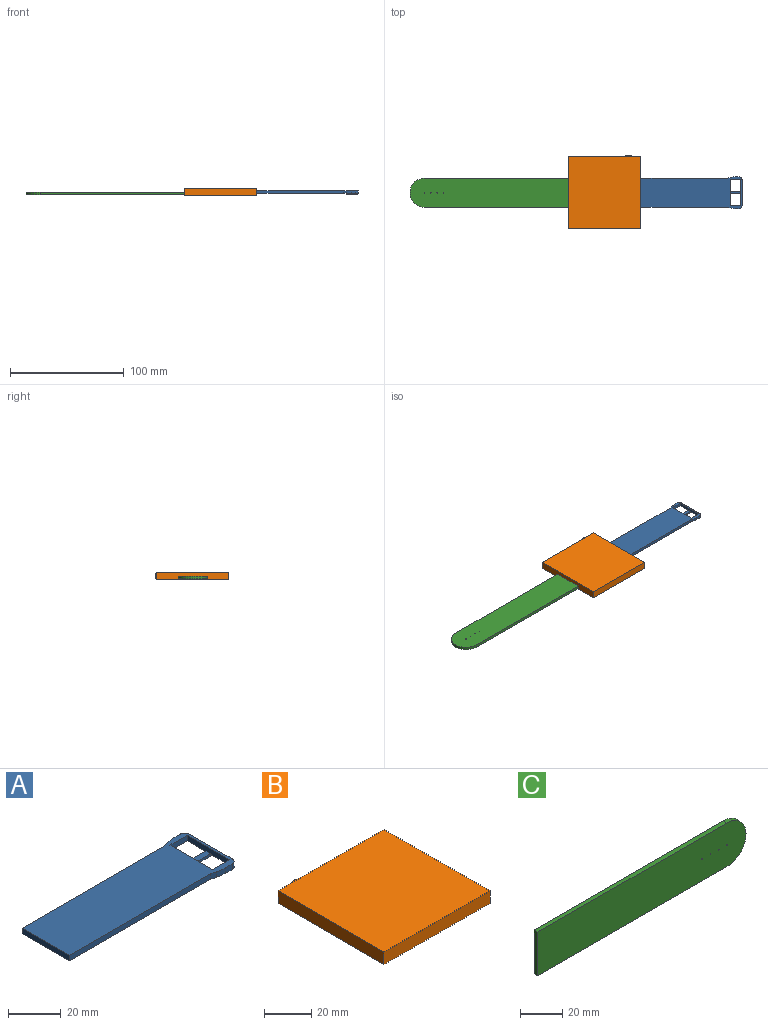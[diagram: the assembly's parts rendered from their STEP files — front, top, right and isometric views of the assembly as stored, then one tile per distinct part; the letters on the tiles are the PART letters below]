
ASSEMBLY  parts=3 mates=2
PART A: 24 faces, bbox 88.9x27.9x3.3 mm
  f0: plane 22.82x2.54mm, normal (-1,0,0), area 57.3mm2, adj f1,f2,f12,f13,f14,f15,f16
  f1: plane 88.9x27.94mm, normal (0,0,1), area 2071.9mm2, adj f0,f3,f4,f5,f6,f7,f8,f9
  f2: plane 88.9x27.94mm, normal (0,0,-1), area 2069.5mm2, adj f0,f3,f4,f5,f6,f7,f8,f9
  f3: plane 76.2x2.54mm, normal (0,-1,0), area 193.5mm2, adj f1,f2,f4,f10
  f4: plane 2.54x2.41mm, normal (-0.27,-0.96,0), area 6.4mm2, adj f1,f2,f3,f23
  f5: plane 3.33x2.54mm, normal (0,-1,0), area 8.5mm2, adj f1,f2,f20,f23
  f6: plane 22.86x2.54mm, normal (1,0,0), area 58.1mm2, adj f1,f2,f20,f21
  f7: plane 3.33x2.54mm, normal (0,1,0), area 8.5mm2, adj f1,f2,f21,f22
  f8: plane 2.54x2.41mm, normal (-0.27,0.96,0), area 6.4mm2, adj f1,f2,f9,f22
  f9: plane 76.2x2.54mm, normal (0,1,0), area 193.5mm2, adj f1,f2,f8,f10
  f10: plane 25.4x2.54mm, normal (-1,0,0), area 64.5mm2, adj f1,f2,f3,f9
  f11: plane 22.82x2.54mm, normal (1,0,0), area 57.3mm2, adj f1,f2,f12,f13,f14,f15,f16
  f12: plane 9.18x2.54mm, normal (0,1,0), area 23.3mm2, adj f0,f1,f2,f11
  f13: plane 9.18x2.54mm, normal (0,-1,0), area 23.3mm2, adj f0,f1,f2,f11
  f14: plane 10.12x1.02mm, normal (0,1,0), area 10mm2, adj f0,f2,f11,f16,f17,f18,f19
  f15: plane 10.12x1.02mm, normal (0,-1,0), area 10mm2, adj f0,f2,f11,f16,f17,f18,f19
  f16: plane 9.18x2.54mm, normal (0,0,1), area 23.3mm2, adj f0,f11,f14,f15
  f17: plane 2.54x0.76mm, normal (-1,0,0), area 1.9mm2, adj f2,f14,f15,f19
  f18: plane 2.54x0.76mm, normal (1,0,0), area 1.9mm2, adj f2,f14,f15,f19
  f19: plane 10.12x2.54mm, normal (0,0,-1), area 25.7mm2, adj f14,f15,f17,f18
  f20: cylinder r=2.54mm len=2.54mm, axis (0,0,-1), area 10.1mm2, adj f1,f2,f5,f6
  f21: cylinder r=2.54mm len=2.54mm, axis (0,0,-1), area 10.1mm2, adj f1,f2,f6,f7
  f22: cylinder r=16.51mm len=4.41mm, axis (0,0,-1), area 11.3mm2, adj f1,f2,f7,f8
  f23: cylinder r=16.51mm len=4.41mm, axis (0,0,-1), area 11.3mm2, adj f1,f2,f4,f5
PART B: 8 faces, bbox 63.5x64.8x6.5 mm
  f0: plane 63.5x6.48mm, normal (0,-1,0), area 411.3mm2, adj f1,f3,f4,f5
  f1: plane 63.5x6.48mm, normal (1,0,0), area 411.3mm2, adj f0,f2,f4,f5
  f2: plane 63.5x6.48mm, normal (0,1,0), area 391mm2, adj f1,f3,f4,f5,f6
  f3: plane 63.5x6.48mm, normal (-1,0,0), area 411.3mm2, adj f0,f2,f4,f5
  f4: plane 63.5x63.5mm, normal (0,0,1), area 4032.3mm2, adj f0,f1,f2,f3
  f5: plane 63.5x63.5mm, normal (0,0,-1), area 4032.3mm2, adj f0,f1,f2,f3
  f6: cylinder r=2.54mm len=5.08mm, axis (0,-1,0), area 21.3mm2, adj f2,f7
  f7: plane 5.08x5.08mm, normal (0,1,0), area 20.3mm2, adj f6
PART C: 10 faces, bbox 139.6x2.5x25.4 mm
  f0: cylinder r=12.7mm len=25.4mm, axis (0,1,0), area 101.3mm2, adj f1,f6,f8,f9
  f1: plane 127x2.54mm, normal (0,0,1), area 322.6mm2, adj f0,f2,f8,f9
  f2: plane 25.4x2.54mm, normal (-1,0,0), area 64.5mm2, adj f1,f6,f8,f9
  f3: cylinder r=0.25mm len=2.54mm, axis (0,1,0), area 4mm2, adj f8,f9
  f4: cylinder r=0.25mm len=2.54mm, axis (0,1,0), area 4mm2, adj f8,f9
  f5: cylinder r=0.25mm len=2.54mm, axis (0,1,0), area 4mm2, adj f8,f9
  f6: plane 126.79x2.54mm, normal (0,0,-1), area 322mm2, adj f0,f2,f8,f9
  f7: cylinder r=0.25mm len=2.54mm, axis (0,1,0), area 4mm2, adj f8,f9
  f8: plane 139.6x25.4mm, normal (0,-1,0), area 3475.7mm2, adj f0,f1,f2,f3,f4,f5,f6,f7
  f9: plane 139.6x25.4mm, normal (0,1,0), area 3475.7mm2, adj f0,f1,f2,f3,f4,f5,f6,f7
PLACE A at identity
PLACE B rot(axis=(0,1,0),180deg) t=(-76.2,0,4.51)mm fixed
PLACE C rot(axis=(0,-0.71,0.71),180deg) t=(-138.73,0,-1.27)mm
MATE fastened C.f2 <-> B.f1  axis (1,0,0) through (-107.95,0,1.27)mm
MATE fastened B.f3 <-> A.f10  axis (1,0,0) through (-44.45,0,1.27)mm
